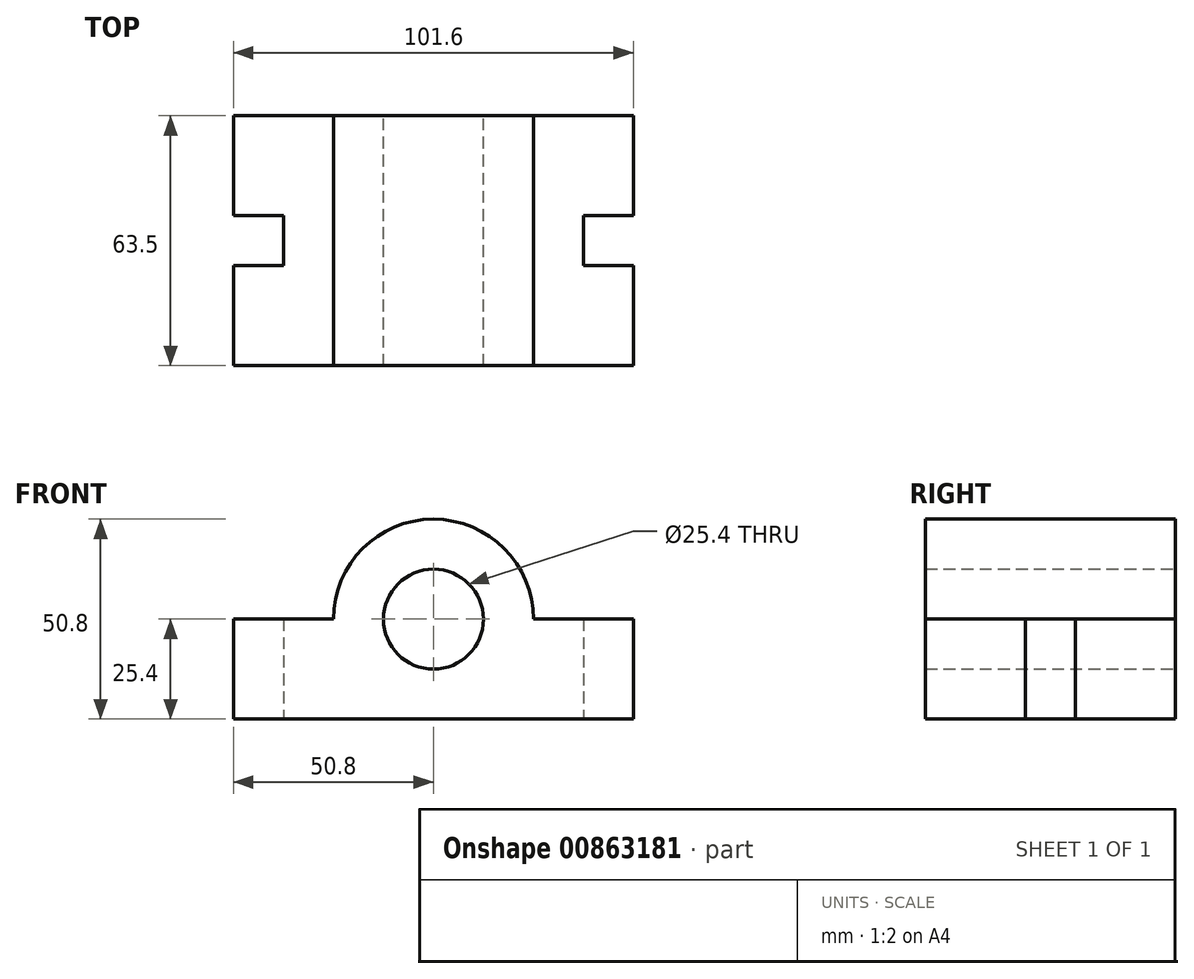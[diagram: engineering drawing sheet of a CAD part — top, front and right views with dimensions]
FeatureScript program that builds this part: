
annotation { "Feature Type Name" : "Feature", "Feature Type Description" : "" }
export const myFeature = defineFeature(function(context is Context, id is Id, definition is map)
    precondition{}
    {
        {
            var Q0;
            Q0=qCreatedBy(makeId("Front.planeOp"),FACE);
            var sketch = newSketch(context, id + "F0", { "sketchPlane" : qUnion([Q0])});
            skLineSegment(sketch, "E0", {"start": v(0, 0) * mm, "end": v(101.6, 0) * mm});
            skLineSegment(sketch, "E1", {"start": v(101.6, 0) * mm, "end": v(101.6, 25.4) * mm});
            skLineSegment(sketch, "E2", {"start": v(0, 0) * mm, "end": v(0, 25.4) * mm});
            skCircle(sketch, "E3", {"center": v(50.8, 25.4) * mm, "radius": 12.7 * mm});
            skPoint(sketch, "E3.centerSnap0", {"position": v(50.8, 0) * mm});
            skArc(sketch, "E4", {"start": v(76.2, 25.4) * mm, "mid": v(50.8, 50.8) * mm, "end": v(25.4, 25.4) * mm});
            skLineSegment(sketch, "E5", {"start": v(0, 25.4) * mm, "end": v(25.4, 25.4) * mm});
            skLineSegment(sketch, "E6", {"start": v(101.6, 25.4) * mm, "end": v(76.2, 25.4) * mm});
            skSolve(sketch);
        }
        {
            var Q0;
            Q0 = qSketchRegion(id + "F0", true);
            extrude(context, id + "F1", {"entities" : qUnion([Q0]), "depth" : 63.5 * mm, "offsetDistance" : 25.4 * mm});
        }
        {
            var Q0;
            Q0=qCreatedBy(makeId("Top.planeOp"),FACE);
            var sketch = newSketch(context, id + "F2", { "sketchPlane" : qUnion([Q0])});
            skLineSegment(sketch, "E7", {"start": v(0, -25.4) * mm, "end": v(12.7, -25.4) * mm});
            skLineSegment(sketch, "E8", {"start": v(12.7, -25.4) * mm, "end": v(12.7, -38.1) * mm});
            skLineSegment(sketch, "E9", {"start": v(12.7, -38.1) * mm, "end": v(0, -38.1) * mm});
            skLineSegment(sketch, "E10", {"start": v(0, -25.4) * mm, "end": v(0, -38.1) * mm});
            skLineSegment(sketch, "E11", {"start": v(101.6, -25.4) * mm, "end": v(88.9, -25.4) * mm});
            skLineSegment(sketch, "E12", {"start": v(88.9, -25.4) * mm, "end": v(88.9, -38.1) * mm});
            skLineSegment(sketch, "E13", {"start": v(88.9, -38.1) * mm, "end": v(101.6, -38.1) * mm});
            skLineSegment(sketch, "E14", {"start": v(101.6, -25.4) * mm, "end": v(101.6, -38.1) * mm});
            skSolve(sketch);
        }
        {
            var Q0;
            Q0 = qSketchRegion(id + "F2", true);
            extrude(context, id + "F3", {"entities" : qUnion([Q0]), "operationType" : NewBodyOperationType.REMOVE, "endBound" : BoundingType.THROUGH_ALL, "depth" : 25.4 * mm, "offsetDistance" : 25.4 * mm});
        }
    });
